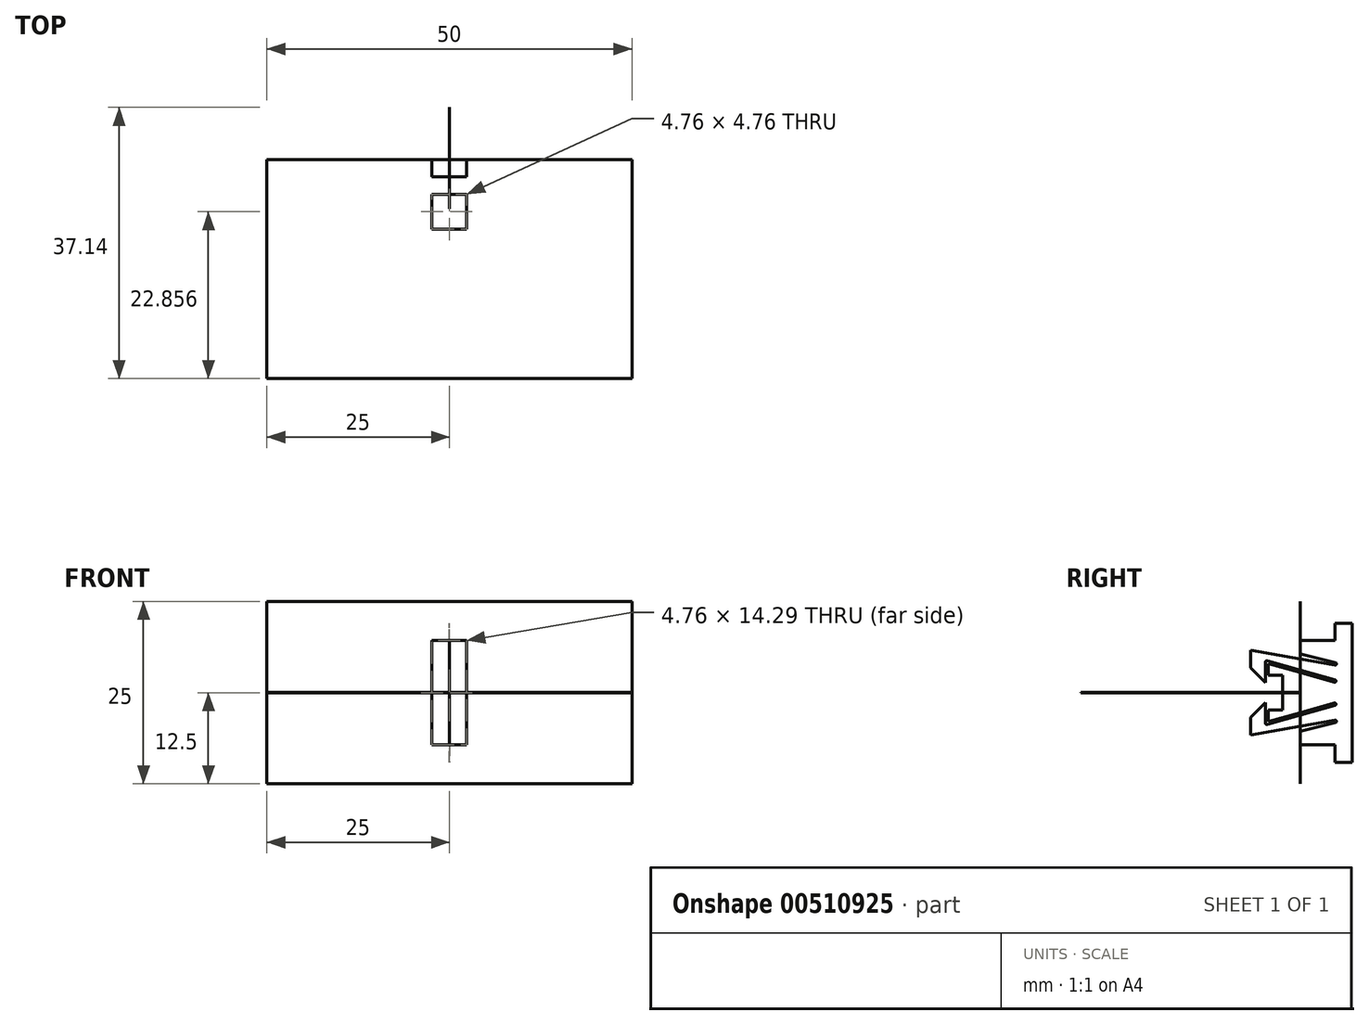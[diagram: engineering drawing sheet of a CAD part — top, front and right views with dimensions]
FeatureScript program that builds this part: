
annotation { "Feature Type Name" : "Feature", "Feature Type Description" : "" }
export const myFeature = defineFeature(function(context is Context, id is Id, definition is map)
    precondition{}
    {
        {
            assignVariable(context, id + "F0", {"name" : "thick", "anyValue" : 3 / 406.4 * mm});
        }
        {
            var Q0;
            Q0=qCreatedBy(makeId("Top.planeOp"),FACE);
            var sketch = newSketch(context, id + "F1", { "sketchPlane" : qUnion([Q0])});
            skLineSegment(sketch, "E0", {"start": v(0, 0) * mm, "end": v(0, -30) * mm, "construction": true});
            skLineSegment(sketch, "E1", {"start": v(-25, 0) * mm, "end": v(-2.38, 0) * mm});
            skLineSegment(sketch, "E2", {"start": v(-2.38, 0) * mm, "end": v(-2.38, -2.38) * mm});
            skLineSegment(sketch, "E3", {"start": v(-2.38, -2.38) * mm, "end": v(0, -2.38) * mm});
            skLineSegment(sketch, "E4", {"start": v(0, -4.76) * mm, "end": v(-2.38, -4.76) * mm});
            skLineSegment(sketch, "E5", {"start": v(-2.38, -4.76) * mm, "end": v(-2.38, -9.53) * mm});
            skLineSegment(sketch, "E6", {"start": v(-2.38, -9.53) * mm, "end": v(0, -9.53) * mm});
            skLineSegment(sketch, "E7", {"start": v(0, -2.38) * mm, "end": v(0, -4.76) * mm, "construction": true});
            skLineSegment(sketch, "E8", {"start": v(-2.38, 0) * mm, "end": v(-2.38, -4.76) * mm, "construction": true});
            skLineSegment(sketch, "E9", {"start": v(-25, 0) * mm, "end": v(-25, -30) * mm});
            skLineSegment(sketch, "E10", {"start": v(-25, -30) * mm, "end": v(0, -30) * mm});
            skLineSegment(sketch, "E11.MirrorCS", {"start": v(25, -30) * mm, "end": v(0, -30) * mm});
            skLineSegment(sketch, "E12.MirrorCS", {"start": v(25, 0) * mm, "end": v(25, -30) * mm});
            skLineSegment(sketch, "E13.MirrorCS", {"start": v(2.38, -9.53) * mm, "end": v(0, -9.53) * mm});
            skLineSegment(sketch, "E14.MirrorCS", {"start": v(2.38, -4.76) * mm, "end": v(2.38, -9.53) * mm});
            skLineSegment(sketch, "E15.MirrorCS", {"start": v(0, -4.76) * mm, "end": v(2.38, -4.76) * mm});
            skLineSegment(sketch, "E16.MirrorCS", {"start": v(2.38, 0) * mm, "end": v(2.38, -2.38) * mm});
            skLineSegment(sketch, "E17.MirrorCS", {"start": v(25, 0) * mm, "end": v(2.38, 0) * mm});
            skLineSegment(sketch, "E18.MirrorCS", {"start": v(2.38, -2.38) * mm, "end": v(0, -2.38) * mm});
            skSolve(sketch);
        }
        {
            var Q0;
            Q0=makeQuery(id+"F1.imprint","IMPRINT",FACE,{"disambiguationData":[TD([[makeQuery(id+"F1.imprint","IMPRINT",EDGE,{"derivedFrom":sQuery(id+"F1.wireOp",EDGE,"E1")}),-1.0]])]});
            extrude(context, id + "F2", {"entities" : qUnion([Q0]), "endBound" : BoundingType.SYMMETRIC, "depth" : getVariable(context, 'thick')});
        }
        {
            var Q0;
            Q0=qCreatedBy(makeId("Front.planeOp"),FACE);
            var sketch = newSketch(context, id + "F3", { "sketchPlane" : qUnion([Q0])});
            skLineSegment(sketch, "E19.bottom", {"start": v(-25, 12.5) * mm, "end": v(25, 12.5) * mm});
            skLineSegment(sketch, "E19.top", {"start": v(-25, -12.5) * mm, "end": v(25, -12.5) * mm});
            skLineSegment(sketch, "E19.left", {"start": v(-25, 12.5) * mm, "end": v(-25, -12.5) * mm});
            skLineSegment(sketch, "E19.right", {"start": v(25, 12.5) * mm, "end": v(25, -12.5) * mm});
            skPoint(sketch, "E19.middle", {"position": v(0, 0) * mm});
            skLineSegment(sketch, "E20.bottom", {"start": v(-2.38, -7.14) * mm, "end": v(2.38, -7.14) * mm});
            skLineSegment(sketch, "E20.top", {"start": v(-2.38, 7.14) * mm, "end": v(2.38, 7.14) * mm});
            skLineSegment(sketch, "E20.left", {"start": v(-2.38, -7.14) * mm, "end": v(-2.38, 7.14) * mm});
            skLineSegment(sketch, "E20.right", {"start": v(2.38, -7.14) * mm, "end": v(2.38, 7.14) * mm});
            skSolve(sketch);
        }
        {
            var Q0;
            Q0=makeQuery(id+"F3.imprint","IMPRINT",FACE,{"disambiguationData":[TD([[makeQuery(id+"F3.imprint","IMPRINT",EDGE,{"derivedFrom":sQuery(id+"F3.wireOp",EDGE,"E19.bottom")}),-1.0]])]});
            extrude(context, id + "F4", {"entities" : qUnion([Q0]), "oppositeDirection" : true, "depth" : getVariable(context, 'thick')});
        }
        {
            var Q0;
            Q0=qCreatedBy(makeId("Right.planeOp"),FACE);
            var sketch = newSketch(context, id + "F5", { "sketchPlane" : qUnion([Q0])});
            skLineSegment(sketch, "E21", {"start": v(0, 0) * mm, "end": v(-33.58, 0) * mm, "construction": true});
            skLineSegment(sketch, "E22", {"start": v(4.76, 7.14) * mm, "end": v(4.76, 9.53) * mm});
            skLineSegment(sketch, "E23", {"start": v(4.76, 9.53) * mm, "end": v(7.14, 9.53) * mm});
            skLineSegment(sketch, "E24", {"start": v(7.14, 9.53) * mm, "end": v(7.14, 0) * mm});
            skLineSegment(sketch, "E25.0", {"start": v(-4.76, 2.38) * mm, "end": v(-4.76, -2.38) * mm, "construction": true});
            skLineSegment(sketch, "E26", {"start": v(-4.76, 2.38) * mm, "end": v(-4.76, 1.38) * mm});
            skLineSegment(sketch, "E27", {"start": v(-4.76, 1.38) * mm, "end": v(-6.76, 3.38) * mm});
            skLineSegment(sketch, "E28.0", {"start": v(-2.38, 2.38) * mm, "end": v(-2.38, -2.38) * mm});
            skLineSegment(sketch, "E29", {"start": v(-2.38, 2.38) * mm, "end": v(-4.4, 2.38) * mm});
            skLineSegment(sketch, "E30", {"start": v(-4.4, 2.38) * mm, "end": v(-4.4, 3.97) * mm});
            skLineSegment(sketch, "E31", {"start": v(-4.4, 3.97) * mm, "end": v(4.67, 1.43) * mm});
            skLineSegment(sketch, "E32", {"start": v(-4.76, 2.38) * mm, "end": v(-4.76, 4.2) * mm});
            skLineSegment(sketch, "E33", {"start": v(-4.54, 4.37) * mm, "end": v(4.76, 1.77) * mm});
            skLineSegment(sketch, "E34", {"start": v(-6.76, 3.38) * mm, "end": v(-6.76, 5.79) * mm});
            skLineSegment(sketch, "E35", {"start": v(-6.76, 5.79) * mm, "end": v(4.76, 3.77) * mm});
            skLineSegment(sketch, "E36", {"start": v(-4.76, 4.44) * mm, "end": v(-4.76, 5.44) * mm, "construction": true});
            skLineSegment(sketch, "E37", {"start": v(4.76, 1.77) * mm, "end": v(4.76, 2.77) * mm, "construction": true});
            skLineSegment(sketch, "E38", {"start": v(4.76, 2.77) * mm, "end": v(4.76, 3.77) * mm, "construction": true});
            skLineSegment(sketch, "E39", {"start": v(4.76, 7.14) * mm, "end": v(0, 7.14) * mm});
            skLineSegment(sketch, "E40", {"start": v(0, 7.14) * mm, "end": v(0, 5.3) * mm});
            skLineSegment(sketch, "E41", {"start": v(0, 5.3) * mm, "end": v(4.84, 4.12) * mm});
            skArc(sketch, "E42", {"start": v(4.76, 3.77) * mm, "mid": v(4.97, 3.9) * mm, "end": v(4.84, 4.12) * mm});
            skArc(sketch, "E43", {"start": v(4.67, 1.43) * mm, "mid": v(4.89, 1.55) * mm, "end": v(4.76, 1.77) * mm});
            skLineSegment(sketch, "E44", {"start": v(-2.38, 0) * mm, "end": v(-2.38, 2.38) * mm});
            skLineSegment(sketch, "E45", {"start": v(0, 5.3) * mm, "end": v(0, 4.6) * mm, "construction": true});
            skLineSegment(sketch, "E46", {"start": v(0, 5.3) * mm, "end": v(-4.52, 6.4) * mm, "construction": true});
            skLineSegment(sketch, "E47", {"start": v(-4.76, 5.44) * mm, "end": v(-4.52, 6.4) * mm, "construction": true});
            skPoint(sketch, "E48.visualSharp", {"position": v(-4.76, 4.44) * mm});
            skArc(sketch, "E48.filletArc", {"start": v(-4.54, 4.37) * mm, "mid": v(-4.7, 4.34) * mm, "end": v(-4.76, 4.2) * mm});
            skLineSegment(sketch, "E49.MirrorCS", {"start": v(-4.76, -2.38) * mm, "end": v(-4.76, -1.38) * mm});
            skArc(sketch, "E50.MirrorCS", {"start": v(-4.54, -4.37) * mm, "mid": v(-4.7, -4.34) * mm, "end": v(-4.76, -4.2) * mm});
            skLineSegment(sketch, "E51.MirrorCS", {"start": v(-4.76, -4.44) * mm, "end": v(-4.76, -5.44) * mm, "construction": true});
            skArc(sketch, "E52.MirrorCS", {"start": v(4.67, -1.43) * mm, "mid": v(4.89, -1.55) * mm, "end": v(4.76, -1.77) * mm});
            skArc(sketch, "E53.MirrorCS", {"start": v(4.76, -3.77) * mm, "mid": v(4.97, -3.9) * mm, "end": v(4.84, -4.12) * mm});
            skLineSegment(sketch, "E54.MirrorCS", {"start": v(4.76, -2.77) * mm, "end": v(4.76, -3.77) * mm, "construction": true});
            skLineSegment(sketch, "E55.MirrorCS", {"start": v(-4.76, -5.44) * mm, "end": v(-4.52, -6.4) * mm, "construction": true});
            skLineSegment(sketch, "E56.MirrorCS", {"start": v(4.76, -1.77) * mm, "end": v(4.76, -2.77) * mm, "construction": true});
            skLineSegment(sketch, "E57.MirrorCS", {"start": v(-4.4, -2.38) * mm, "end": v(-4.4, -3.97) * mm});
            skLineSegment(sketch, "E58.MirrorCS", {"start": v(0, -5.3) * mm, "end": v(0, -4.6) * mm, "construction": true});
            skPoint(sketch, "E59.MirrorP", {"position": v(-4.76, -4.44) * mm});
            skLineSegment(sketch, "E60.MirrorCS", {"start": v(-4.76, -2.38) * mm, "end": v(-4.76, 2.38) * mm, "construction": true});
            skLineSegment(sketch, "E61.MirrorCS", {"start": v(0, -5.3) * mm, "end": v(-4.52, -6.4) * mm, "construction": true});
            skLineSegment(sketch, "E62.MirrorCS", {"start": v(-2.38, 0) * mm, "end": v(-2.38, -2.38) * mm});
            skLineSegment(sketch, "E63.MirrorCS", {"start": v(4.76, -7.14) * mm, "end": v(0, -7.14) * mm});
            skLineSegment(sketch, "E64.MirrorCS", {"start": v(0, -5.3) * mm, "end": v(4.84, -4.12) * mm});
            skLineSegment(sketch, "E65.MirrorCS", {"start": v(-2.38, -2.38) * mm, "end": v(-2.38, 2.38) * mm});
            skLineSegment(sketch, "E66.MirrorCS", {"start": v(0, -7.14) * mm, "end": v(0, -5.3) * mm});
            skLineSegment(sketch, "E67.MirrorCS", {"start": v(-4.76, -1.38) * mm, "end": v(-6.76, -3.38) * mm});
            skLineSegment(sketch, "E68.MirrorCS", {"start": v(-4.76, -2.38) * mm, "end": v(-4.76, -4.2) * mm});
            skLineSegment(sketch, "E69.MirrorCS", {"start": v(-4.4, -3.97) * mm, "end": v(4.67, -1.43) * mm});
            skLineSegment(sketch, "E70.MirrorCS", {"start": v(-4.54, -4.37) * mm, "end": v(4.76, -1.77) * mm});
            skLineSegment(sketch, "E71.MirrorCS", {"start": v(-6.76, -3.38) * mm, "end": v(-6.76, -5.79) * mm});
            skLineSegment(sketch, "E72.MirrorCS", {"start": v(4.76, -7.14) * mm, "end": v(4.76, -9.53) * mm});
            skLineSegment(sketch, "E73.MirrorCS", {"start": v(-2.38, -2.38) * mm, "end": v(-4.4, -2.38) * mm});
            skLineSegment(sketch, "E74.MirrorCS", {"start": v(4.76, -9.53) * mm, "end": v(7.14, -9.53) * mm});
            skLineSegment(sketch, "E75.MirrorCS", {"start": v(-6.76, -5.79) * mm, "end": v(4.76, -3.77) * mm});
            skLineSegment(sketch, "E76.MirrorCS", {"start": v(7.14, -9.53) * mm, "end": v(7.14, 0) * mm});
            skLineSegment(sketch, "E77", {"start": v(4.71, -1.6) * mm, "end": v(4.71, 1.6) * mm, "construction": true});
            skLineSegment(sketch, "E78", {"start": v(4.76, 7.14) * mm, "end": v(4.8, 3.95) * mm, "construction": true});
            skLineSegment(sketch, "E79", {"start": v(-7.26, -2.38) * mm, "end": v(-9.53, -4.64) * mm});
            skLineSegment(sketch, "E80", {"start": v(-9.53, -4.64) * mm, "end": v(-9.53, 0) * mm});
            skLineSegment(sketch, "E81", {"start": v(-7.26, -2.38) * mm, "end": v(-7.26, 0) * mm});
            skLineSegment(sketch, "E82.MirrorCS", {"start": v(-9.53, 4.64) * mm, "end": v(-9.53, 0) * mm});
            skLineSegment(sketch, "E83.MirrorCS", {"start": v(-7.26, 2.38) * mm, "end": v(-7.26, 0) * mm});
            skLineSegment(sketch, "E84.MirrorCS", {"start": v(-7.26, 2.38) * mm, "end": v(-9.53, 4.64) * mm});
            skSolve(sketch);
        }
        {
            var Q0;
            Q0=makeQuery(id+"F5.imprint","IMPRINT",FACE,{"disambiguationData":[TD([[makeQuery(id+"F5.imprint","IMPRINT",EDGE,{"derivedFrom":sQuery(id+"F5.wireOp",EDGE,"E22")}),-1.0]])]});
            extrude(context, id + "F6", {"entities" : qUnion([Q0]), "endBound" : BoundingType.SYMMETRIC, "depth" : getVariable(context, 'thick')});
        }
    });
